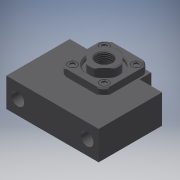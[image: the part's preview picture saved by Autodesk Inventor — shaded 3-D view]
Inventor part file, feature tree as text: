
AUTODESK INVENTOR PART (.ipt)
format: ipt  version: 2018 (Build 220112000, 112)  size: 376,832 bytes
history: native  units: mm
features: sketch x23, other x14, revolve x12, extrude x9, pattern_linear x3, hole x2, thread x1
ambient origin geometry x8: Origin, YZ Plane, XZ Plane, XY Plane, X Axis, Y Axis, Z Axis, Center Point
bodies: Solid1 (feature_tree)
feature tree (64):
  extrude  "Extrusion1"  Depth=2.5mm TaperAngle=0.0deg
  extrude  "Extrusion2"  Depth=8.5mm TaperAngle=0.0deg
  revolve  "Revolution1"  Angle=360.0deg
  extrude  "Extrusion3"  TaperAngle=360.0deg  [1 undecoded]
  extrude  "Extrusion4"  TaperAngle=360.0deg  [1 undecoded]
  revolve  "Revolution2"  [1 undecoded]
  hole  "Hole5"  [1 undecoded]
  revolve  "Revolution3"  [1 undecoded]
  thread  "Thread1"  [1 undecoded]
  revolve  "Revolution4"  [1 undecoded]
  revolve  "Revolution5"  Angle=360.0deg
  pattern_linear  "Rectangular Pattern1"  Count1=8  [1 undecoded]
  revolve  "Revolution6"  [1 undecoded]
  pattern_linear  "Rectangular Pattern2"  Spacing1=10.0mm  [1 undecoded]
  extrude  "Extrusion5"  [1 undecoded]
  pattern_linear  "Rectangular Pattern3"  [2 undecoded]
  revolve  "Revolution7"  [1 undecoded]
  revolve  "Revolution8"  [1 undecoded]
  extrude  "Extrusion6"  [1 undecoded]
  revolve  "Revolution9"  [1 undecoded]
  revolve  "Revolution10"  [1 undecoded]
  extrude  "Extrusion7"  [1 undecoded]
  extrude  "Extrusion8"  [1 undecoded]
  revolve  "Revolution11"  [1 undecoded]
  revolve  "Revolution12"  [1 undecoded]
  extrude  "Extrusion9"  [1 undecoded]
  other  "unit_XY"
  other  "unit_YZ"
  other  "unit_ZX"
  other  "unit_X"
  other  "unit_Y"
  other  "unit_Z"
  other  "unit_Center"
  other  "unit_collar_XY"
  other  "unit_collar_YZ"
  other  "unit_collar_ZX"
  other  "unit_collar_X"
  other  "unit_collar_Y"
  other  "unit_collar_Z"
  other  "unit_collar_Center"
  hole  "Hole6"  [1 undecoded]
  sketch  "Sketch_1"  dims[d0=25.0mm d1=0.0mm d30=2.5mm d31=0.0mm]
  sketch  "Sketch_10"  dims[d32=360.0deg d33=8.5mm d34=0.0mm]
  sketch  "Sketch_13"  dims[d49=360.0deg d50=20.0mm d52=27.577164mm d53=20.0mm d55=27.577164mm]
  sketch  "Sketch_11"  dims[d35=3.5mm d36=0.0mm d37=360.0deg]
  sketch  "Sketch_12"  dims[d46=6.876mm d47=0.0mm d48=360.0deg]
  sketch  "Sketch_14"  dims[d56=360.0deg d57=20.0mm d59=27.577164mm d60=20.0mm d62=27.577164mm]
  sketch  "Sketch11"  dims[d38=15.0mm d39=6.0mm d40=19.5mm d41=6.0mm d42=90.0deg d43=30.0mm d44=0.0mm d45=360.0deg]
  sketch  "Sketch_16"  dims[d63=1.2mm d64=0.0mm d65=20.0mm d67=27.577164mm d68=20.0mm d70=27.577164mm d71=360.0deg]
  sketch  "Sketch_17"  dims[d72=360.0deg d73=1.2mm d74=0.0mm]
  sketch  "Sketch_18"  dims[d75=360.0deg d76=360.0deg]
  sketch  "Sketch_20"  dims[d77=16.0mm d78=0.0mm]
  sketch  "Sketch_22"  dims[d79=6.0mm d80=0.0mm]
  sketch  "Sketch_24"  dims[d81=360.0deg]
  sketch  "Sketch_25"  dims[d82=360.0deg]
  sketch  "Sketch_26"  dims[d83=0.01mm d84=0.0mm]
  sketch  "Sketch_28"  dims[d90=19.5mm d91=55.0mm]
  sketch  "Sketch_29"  dims[d92=19.5mm]
  sketch  "Sketch_33"  dims[d97=10.0mm d98=10.0mm d99=11.0mm d100=6.0mm d101=17.0mm d102=15.0mm d103=90.0deg d104=8.0mm d105=20.594885mm]
  sketch  "Sketch_27"  dims[d85=0.0mm]
  sketch  "Sketch_30"  dims[d93=10.0mm]
  sketch  "Sketch_31"  dims[d94=41.0mm]
  sketch  "Sketch_32"  dims[d95=10.0mm]
  sketch  "Sketch27"  dims[d86=0.0mm d89=80.0mm]
note: 24 required parameter values undecoded (feature->parameter linkage not recoverable at this tier; creation-order binding heuristic only, values carry confidence <= 0.55)